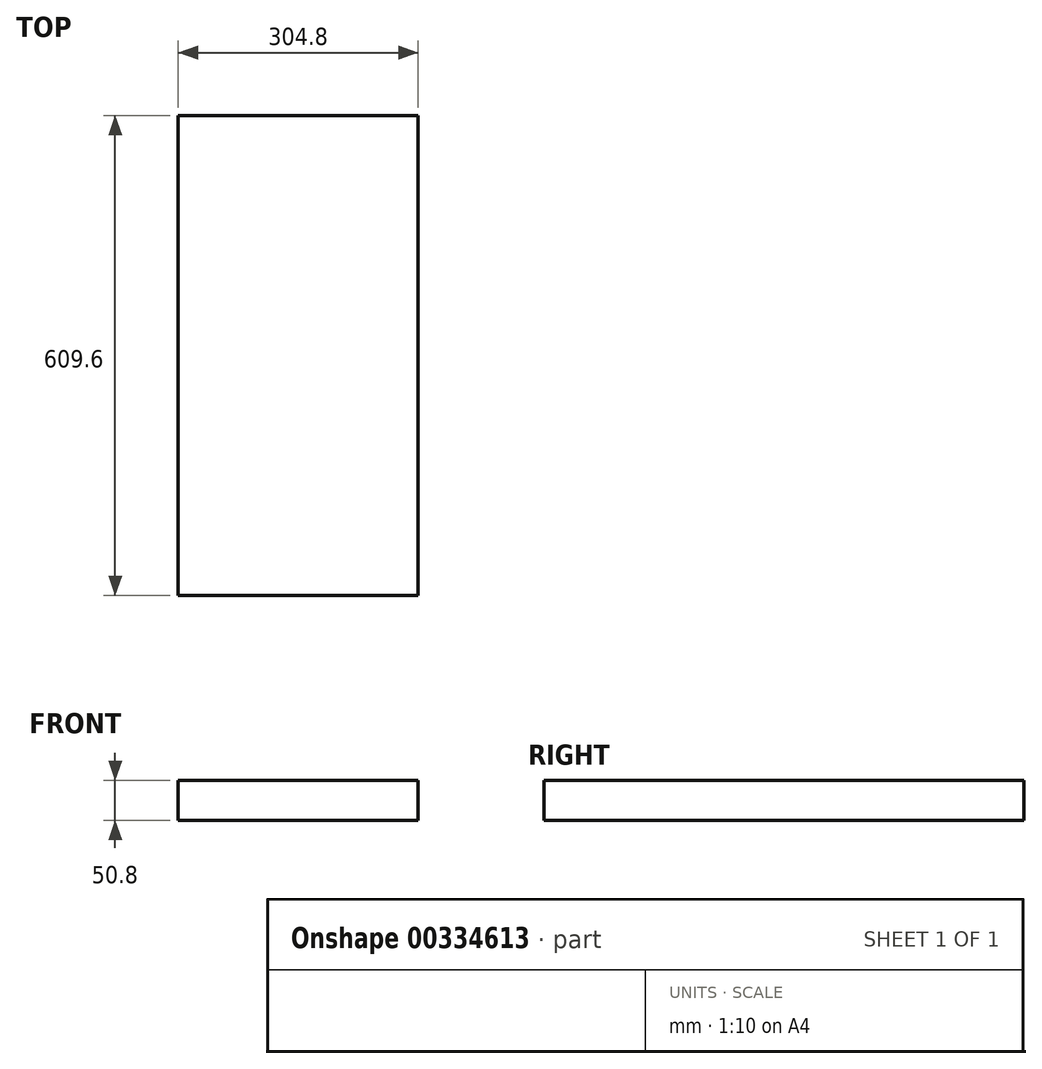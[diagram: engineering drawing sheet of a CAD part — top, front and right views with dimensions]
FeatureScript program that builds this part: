
annotation { "Feature Type Name" : "Feature", "Feature Type Description" : "" }
export const myFeature = defineFeature(function(context is Context, id is Id, definition is map)
    precondition{}
    {
        {
            var Q0;
            Q0=qCreatedBy(makeId("Top.planeOp"),FACE);
            var sketch = newSketch(context, id + "F0", { "sketchPlane" : qUnion([Q0])});
            skLineSegment(sketch, "E0.bottom", {"start": v(-157.81, 382.04) * mm, "end": v(146.99, 382.04) * mm});
            skLineSegment(sketch, "E0.top", {"start": v(-157.81, -227.56) * mm, "end": v(146.99, -227.56) * mm});
            skLineSegment(sketch, "E0.left", {"start": v(-157.81, 382.04) * mm, "end": v(-157.81, -227.56) * mm});
            skLineSegment(sketch, "E0.right", {"start": v(146.99, 382.04) * mm, "end": v(146.99, -227.56) * mm});
            skSolve(sketch);
        }
        {
            var Q0;
            Q0=makeQuery(id+"F0.imprint","IMPRINT",FACE,{"disambiguationData":[TD([[makeQuery(id+"F0.imprint","IMPRINT",EDGE,{"derivedFrom":sQuery(id+"F0.wireOp",EDGE,"E0.bottom")}),-1.0]])]});
            extrude(context, id + "F1", {"entities" : qUnion([Q0]), "depth" : 50.8 * mm});
        }
    });
